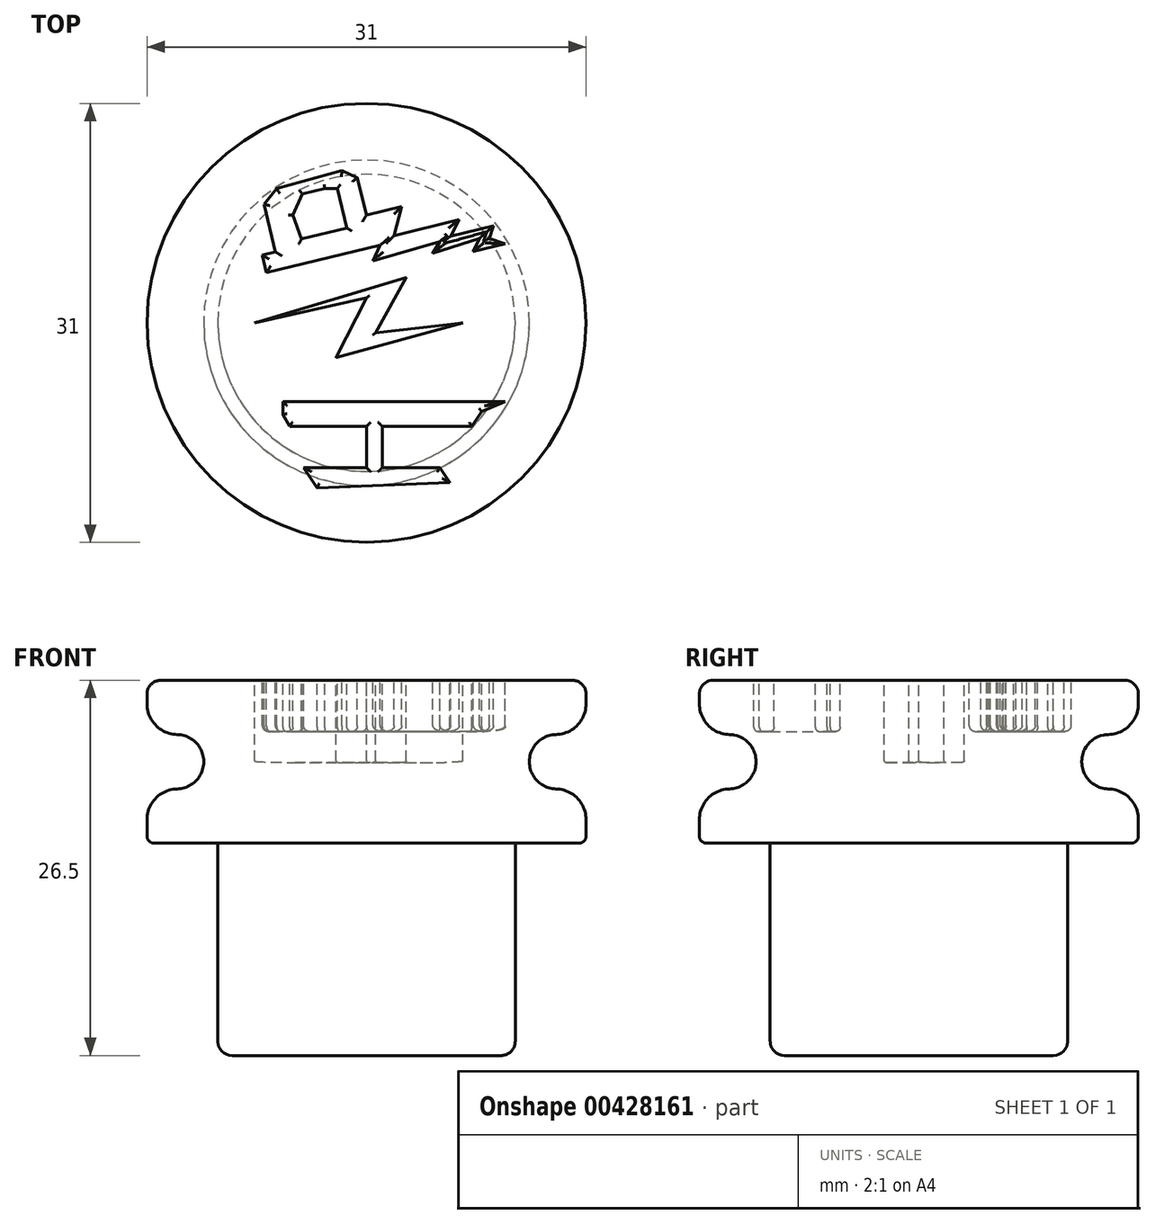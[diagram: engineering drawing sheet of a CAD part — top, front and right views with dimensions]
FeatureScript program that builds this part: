
annotation { "Feature Type Name" : "Feature", "Feature Type Description" : "" }
export const myFeature = defineFeature(function(context is Context, id is Id, definition is map)
    precondition{}
    {
        {
            var Q0;
            Q0=qCreatedBy(makeId("Right.planeOp"),FACE);
            var sketch = newSketch(context, id + "F0", { "sketchPlane" : qUnion([Q0])});
            skLineSegment(sketch, "E0", {"start": v(-10.5, -11.5) * mm, "end": v(-10.5, -26.5) * mm});
            skLineSegment(sketch, "E1", {"start": v(-10.5, -26.5) * mm, "end": v(0, -26.5) * mm});
            skLineSegment(sketch, "E2", {"start": v(0, -26.5) * mm, "end": v(0, 0) * mm});
            skLineSegment(sketch, "E3", {"start": v(0, 0) * mm, "end": v(-15.5, 0) * mm});
            skLineSegment(sketch, "E4", {"start": v(-10.5, -11.5) * mm, "end": v(-15.5, -11.5) * mm});
            skLineSegment(sketch, "E5", {"start": v(-15.5, -11.5) * mm, "end": v(-15.5, -7.67) * mm});
            skLineSegment(sketch, "E6", {"start": v(-15.5, 0) * mm, "end": v(-15.5, -3.83) * mm});
            skLineSegment(sketch, "E7", {"start": v(-15.5, -3.83) * mm, "end": v(-11.5, -3.83) * mm});
            skLineSegment(sketch, "E8", {"start": v(-11.5, -3.83) * mm, "end": v(-11.5, -7.67) * mm});
            skLineSegment(sketch, "E9", {"start": v(-11.5, -7.67) * mm, "end": v(-15.5, -7.67) * mm});
            skSolve(sketch);
        }
        {
            var Q0;
            Q0 = qSketchRegion(id + "F0", true);
            var Q1;
            Q1=sQuery(id+"F0.wireOp",EDGE,"E2");
            revolve(context, id + "F1", {"entities" : qUnion([Q0]), "axis" : qUnion([Q1]), "revolveType" : RevolveType.FULL});
        }
        {
            var Q0;
            Q0=makeQuery(id+"F1.opRevolve","SWEPT_EDGE",EDGE,{"disambiguationData":[OSD([sQuery(id+"F0.wireOp",EDGE,"E7"),sQuery(id+"F0.wireOp",EDGE,"E8")])]});
            var Q1;
            Q1=makeQuery(id+"F1.opRevolve","SWEPT_EDGE",EDGE,{"disambiguationData":[OSD([sQuery(id+"F0.wireOp",EDGE,"E8"),sQuery(id+"F0.wireOp",EDGE,"E9")])]});
            fillet(context, id + "F2", {"entities" : qUnion([Q0, Q1]), "radius" : 1.9 * mm, "tangentPropagation" : true, "allowEdgeOverflow" : false});
        }
        {
            var Q0;
            Q0=makeQuery(id+"F1.opRevolve","SWEPT_EDGE",EDGE,{"disambiguationData":[OSD([sQuery(id+"F0.wireOp",EDGE,"E6"),sQuery(id+"F0.wireOp",EDGE,"E7")])]});
            var Q1;
            Q1=makeQuery(id+"F1.opRevolve","SWEPT_EDGE",EDGE,{"disambiguationData":[OSD([sQuery(id+"F0.wireOp",EDGE,"E5"),sQuery(id+"F0.wireOp",EDGE,"E9")])]});
            fillet(context, id + "F3", {"entities" : qUnion([Q0, Q1]), "radius" : 2.17 * mm, "tangentPropagation" : true, "allowEdgeOverflow" : false});
        }
        {
            var Q0;
            Q0=makeQuery(id+"F1.opRevolve","SWEPT_EDGE",EDGE,{"disambiguationData":[OSD([sQuery(id+"F0.wireOp",EDGE,"E3"),sQuery(id+"F0.wireOp",EDGE,"E6")])]});
            fillet(context, id + "F4", {"entities" : qUnion([Q0]), "radius" : 0.97 * mm, "tangentPropagation" : true, "allowEdgeOverflow" : false});
        }
        {
            var Q0;
            Q0=makeQuery(id+"F1.opRevolve","SWEPT_EDGE",EDGE,{"disambiguationData":[OSD([sQuery(id+"F0.wireOp",EDGE,"E4"),sQuery(id+"F0.wireOp",EDGE,"E5")])]});
            fillet(context, id + "F5", {"entities" : qUnion([Q0]), "radius" : 0.5 * mm, "tangentPropagation" : true, "allowEdgeOverflow" : false});
        }
        {
            var Q0;
            Q0=makeQuery(id+"F1.opRevolve","SWEPT_FACE",FACE,{"disambiguationData":[OSD([sQuery(id+"F0.wireOp",EDGE,"E3")])]});
            var sketch = newSketch(context, id + "F6", { "sketchPlane" : qUnion([Q0])});
            skLineSegment(sketch, "E10", {"start": v(-7.9, 0) * mm, "end": v(0, 1.76) * mm});
            skLineSegment(sketch, "E11", {"start": v(2.8, 3.2) * mm, "end": v(-7.9, 0) * mm});
            skLineSegment(sketch, "E12", {"start": v(0, 1.76) * mm, "end": v(-2.15, -2.44) * mm});
            skLineSegment(sketch, "E13", {"start": v(-2.15, -2.44) * mm, "end": v(6.79, 0) * mm});
            skLineSegment(sketch, "E14", {"start": v(2.8, 3.2) * mm, "end": v(0.64, -0.7) * mm});
            skLineSegment(sketch, "E15", {"start": v(0.64, -0.7) * mm, "end": v(6.79, 0) * mm});
            skSolve(sketch);
        }
        {
            var Q0;
            Q0 = qSketchRegion(id + "F6", true);
            extrude(context, id + "F7", {"entities" : qUnion([Q0]), "operationType" : NewBodyOperationType.REMOVE, "oppositeDirection" : true, "depth" : 5.8 * mm});
        }
        {
            var Q0;
            Q0=makeQuery(id+"F7.boolean.opBoolean","COPY",EDGE,{"derivedFrom":makeQuery(id+"F7.opExtrude","CAP_EDGE",EDGE,{"disambiguationData":[OSD([sQuery(id+"F6.wireOp",EDGE,"E12")])],"isStart":false})});
            var Q1;
            Q1=makeQuery(id+"F7.boolean.opBoolean","COPY",EDGE,{"derivedFrom":makeQuery(id+"F7.opExtrude","CAP_EDGE",EDGE,{"disambiguationData":[OSD([sQuery(id+"F6.wireOp",EDGE,"E13")])],"isStart":false})});
            var Q2;
            Q2=makeQuery(id+"F7.boolean.opBoolean","COPY",EDGE,{"derivedFrom":makeQuery(id+"F7.opExtrude","CAP_EDGE",EDGE,{"disambiguationData":[OSD([sQuery(id+"F6.wireOp",EDGE,"E14")])],"isStart":false})});
            var Q3;
            Q3=makeQuery(id+"F7.boolean.opBoolean","COPY",EDGE,{"derivedFrom":makeQuery(id+"F7.opExtrude","CAP_EDGE",EDGE,{"disambiguationData":[OSD([sQuery(id+"F6.wireOp",EDGE,"E15")])],"isStart":false})});
            var Q4;
            Q4=makeQuery(id+"F7.boolean.opBoolean","COPY",EDGE,{"derivedFrom":makeQuery(id+"F7.opExtrude","CAP_EDGE",EDGE,{"disambiguationData":[OSD([sQuery(id+"F6.wireOp",EDGE,"E11")])],"isStart":false})});
            var Q5;
            Q5=makeQuery(id+"F7.boolean.opBoolean","COPY",EDGE,{"derivedFrom":makeQuery(id+"F7.opExtrude","CAP_EDGE",EDGE,{"disambiguationData":[OSD([sQuery(id+"F6.wireOp",EDGE,"E10")])],"isStart":false})});
            fillet(context, id + "F8", {"entities" : qUnion([Q0, Q1, Q2, Q3, Q4, Q5]), "radius" : 0.1 * mm, "tangentPropagation" : true, "allowEdgeOverflow" : false});
        }
        {
            var Q0;
            Q0=makeQuery(id+"F1.opRevolve","SWEPT_FACE",FACE,{"disambiguationData":[OSD([sQuery(id+"F0.wireOp",EDGE,"E3")])]});
            var sketch = newSketch(context, id + "F9", { "sketchPlane" : qUnion([Q0])});
            skLineSegment(sketch, "E16", {"start": v(-3.5, -11.65) * mm, "end": v(-4.43, -10.22) * mm});
            skLineSegment(sketch, "E17", {"start": v(-4.43, -10.22) * mm, "end": v(5.17, -10.22) * mm});
            skLineSegment(sketch, "E18", {"start": v(5.17, -10.22) * mm, "end": v(5.89, -11.27) * mm});
            skLineSegment(sketch, "E19", {"start": v(5.89, -11.27) * mm, "end": v(-3.5, -11.65) * mm});
            skLineSegment(sketch, "E20", {"start": v(0, -10.22) * mm, "end": v(0, -7.31) * mm});
            skLineSegment(sketch, "E21", {"start": v(0, -7.31) * mm, "end": v(1.11, -7.31) * mm});
            skLineSegment(sketch, "E22", {"start": v(1.11, -7.31) * mm, "end": v(1.11, -10.22) * mm});
            skLineSegment(sketch, "E23", {"start": v(0, -7.31) * mm, "end": v(-5.42, -7.31) * mm});
            skLineSegment(sketch, "E24", {"start": v(-5.42, -7.31) * mm, "end": v(-5.91, -6.5) * mm});
            skLineSegment(sketch, "E25", {"start": v(-5.91, -6.5) * mm, "end": v(-5.91, -5.56) * mm});
            skLineSegment(sketch, "E26", {"start": v(-5.91, -5.56) * mm, "end": v(9.78, -5.56) * mm});
            skLineSegment(sketch, "E27", {"start": v(9.78, -5.56) * mm, "end": v(8.14, -6.27) * mm});
            skLineSegment(sketch, "E28", {"start": v(8.14, -6.27) * mm, "end": v(7.42, -7.31) * mm});
            skLineSegment(sketch, "E29", {"start": v(7.42, -7.31) * mm, "end": v(1.11, -7.31) * mm});
            skLineSegment(sketch, "E30", {"start": v(9.78, 5.58) * mm, "end": v(7.53, 5.03) * mm});
            skLineSegment(sketch, "E31", {"start": v(7.53, 5.03) * mm, "end": v(7.97, 5.97) * mm});
            skLineSegment(sketch, "E32", {"start": v(7.97, 5.97) * mm, "end": v(4.68, 4.92) * mm});
            skLineSegment(sketch, "E33", {"start": v(4.68, 4.92) * mm, "end": v(5.17, 5.75) * mm});
            skLineSegment(sketch, "E34", {"start": v(5.17, 5.75) * mm, "end": v(0.45, 4.38) * mm});
            skLineSegment(sketch, "E35", {"start": v(0.45, 4.38) * mm, "end": v(0.95, 5.47) * mm});
            skLineSegment(sketch, "E36", {"start": v(0.95, 5.47) * mm, "end": v(-7.06, 3.55) * mm});
            skLineSegment(sketch, "E37", {"start": v(9.78, 5.58) * mm, "end": v(8.66, 5.97) * mm});
            skPoint(sketch, "E37.endSnap0", {"position": v(8.66, 5.3) * mm});
            skLineSegment(sketch, "E38", {"start": v(8.66, 5.97) * mm, "end": v(8.96, 6.86) * mm});
            skLineSegment(sketch, "E39", {"start": v(8.96, 6.86) * mm, "end": v(5.93, 6.12) * mm});
            skLineSegment(sketch, "E40", {"start": v(5.93, 6.12) * mm, "end": v(6.55, 7.28) * mm});
            skLineSegment(sketch, "E41", {"start": v(6.55, 7.28) * mm, "end": v(1.96, 6.16) * mm});
            skLineSegment(sketch, "E42", {"start": v(1.96, 6.16) * mm, "end": v(2.48, 8.22) * mm});
            skLineSegment(sketch, "E43", {"start": v(2.48, 8.22) * mm, "end": v(0, 7.61) * mm});
            skLineSegment(sketch, "E44", {"start": v(-7.06, 3.55) * mm, "end": v(-7.36, 4.8) * mm});
            skLineSegment(sketch, "E45", {"start": v(-7.36, 4.8) * mm, "end": v(-6.44, 5.01) * mm});
            skLineSegment(sketch, "E46", {"start": v(-6.44, 5.01) * mm, "end": v(-7.25, 8.38) * mm});
            skLineSegment(sketch, "E47", {"start": v(-7.25, 8.38) * mm, "end": v(-6.35, 9.48) * mm});
            skLineSegment(sketch, "E48", {"start": v(0, 7.61) * mm, "end": v(-0.65, 10.26) * mm});
            skLineSegment(sketch, "E49", {"start": v(-0.65, 10.26) * mm, "end": v(-1.74, 10.74) * mm});
            skLineSegment(sketch, "E50", {"start": v(-1.74, 10.74) * mm, "end": v(-6.35, 9.48) * mm});
            skLineSegment(sketch, "E51", {"start": v(-4.6, 5.91) * mm, "end": v(-1.39, 6.7) * mm});
            skLineSegment(sketch, "E52", {"start": v(-1.39, 6.7) * mm, "end": v(-2.07, 9.48) * mm});
            skLineSegment(sketch, "E53", {"start": v(-2.07, 9.48) * mm, "end": v(-2.95, 9.48) * mm});
            skLineSegment(sketch, "E54", {"start": v(-2.95, 9.48) * mm, "end": v(-4.53, 9.1) * mm});
            skLineSegment(sketch, "E55", {"start": v(-4.53, 9.1) * mm, "end": v(-5.2, 7.61) * mm});
            skLineSegment(sketch, "E56", {"start": v(-5.2, 7.61) * mm, "end": v(-4.6, 5.91) * mm});
            skSolve(sketch);
        }
        {
            var Q0;
            Q0=makeQuery(id+"F9.imprint","IMPRINT",FACE,{"disambiguationData":[TD([[makeQuery(id+"F9.imprint","IMPRINT",EDGE,{"derivedFrom":sQuery(id+"F9.wireOp",EDGE,"E30")}),-1.0]])]});
            var Q1;
            Q1=makeQuery(id+"F9.imprint","IMPRINT",FACE,{"disambiguationData":[TD([[makeQuery(id+"F9.imprint","IMPRINT",EDGE,{"derivedFrom":sQuery(id+"F9.wireOp",EDGE,"E21")}),1.0]])]});
            var Q2;
            {var subQ0=sQuery(id+"F9.wireOp",EDGE,"E20");Q2=makeQuery(id+"F9.imprint","IMPRINT",FACE,{"disambiguationData":[TD([[makeQuery(id+"F9.imprint","IMPRINT",EDGE,{"derivedFrom":subQ0}),-1.0]])]});}
            var Q3;
            {var subQ4=sQuery(id+"F9.wireOp",EDGE,"E16");Q3=makeQuery(id+"F9.imprint","IMPRINT",FACE,{"disambiguationData":[TD([[makeQuery(id+"F9.imprint","IMPRINT",EDGE,{"derivedFrom":subQ4}),-1.0]])]});}
            extrude(context, id + "F10", {"entities" : qUnion([Q0, Q1, Q2, Q3]), "operationType" : NewBodyOperationType.REMOVE, "oppositeDirection" : true, "depth" : 3.6 * mm});
        }
        {
            var Q0;
            Q0=makeQuery(id+"F1.opRevolve","SWEPT_EDGE",EDGE,{"disambiguationData":[OSD([sQuery(id+"F0.wireOp",EDGE,"E0"),sQuery(id+"F0.wireOp",EDGE,"E1")])]});
            fillet(context, id + "F11", {"entities" : qUnion([Q0]), "radius" : 1 * mm, "tangentPropagation" : true, "allowEdgeOverflow" : false});
        }
        {
            var Q0;
            Q0=makeQuery(id+"F10.boolean.opBoolean","COPY",EDGE,{"derivedFrom":makeQuery(id+"F10.opExtrude","CAP_EDGE",EDGE,{"disambiguationData":[OSD([sQuery(id+"F9.wireOp",EDGE,"E51")])],"isStart":true})});
            var Q1;
            Q1=makeQuery(id+"F10.boolean.opBoolean","COPY",EDGE,{"derivedFrom":makeQuery(id+"F10.opExtrude","CAP_EDGE",EDGE,{"disambiguationData":[OSD([sQuery(id+"F9.wireOp",EDGE,"E52")])],"isStart":true})});
            var Q2;
            Q2=makeQuery(id+"F10.boolean.opBoolean","COPY",EDGE,{"derivedFrom":makeQuery(id+"F10.opExtrude","CAP_EDGE",EDGE,{"disambiguationData":[OSD([sQuery(id+"F9.wireOp",EDGE,"E53")])],"isStart":true})});
            var Q3;
            Q3=makeQuery(id+"F10.boolean.opBoolean","COPY",EDGE,{"derivedFrom":makeQuery(id+"F10.opExtrude","CAP_EDGE",EDGE,{"disambiguationData":[OSD([sQuery(id+"F9.wireOp",EDGE,"E54")])],"isStart":true})});
            var Q4;
            Q4=makeQuery(id+"F10.boolean.opBoolean","COPY",EDGE,{"derivedFrom":makeQuery(id+"F10.opExtrude","CAP_EDGE",EDGE,{"disambiguationData":[OSD([sQuery(id+"F9.wireOp",EDGE,"E55")])],"isStart":true})});
            var Q5;
            Q5=makeQuery(id+"F10.boolean.opBoolean","COPY",EDGE,{"derivedFrom":makeQuery(id+"F10.opExtrude","CAP_EDGE",EDGE,{"disambiguationData":[OSD([sQuery(id+"F9.wireOp",EDGE,"E56")])],"isStart":true})});
            var Q6;
            Q6=makeQuery(id+"F10.boolean.opBoolean","COPY",EDGE,{"derivedFrom":makeQuery(id+"F10.opExtrude","CAP_EDGE",EDGE,{"disambiguationData":[OSD([sQuery(id+"F9.wireOp",EDGE,"E56")])],"isStart":false})});
            var Q7;
            Q7=makeQuery(id+"F10.boolean.opBoolean","COPY",EDGE,{"derivedFrom":makeQuery(id+"F10.opExtrude","CAP_EDGE",EDGE,{"disambiguationData":[OSD([sQuery(id+"F9.wireOp",EDGE,"E55")])],"isStart":false})});
            var Q8;
            Q8=makeQuery(id+"F10.boolean.opBoolean","COPY",EDGE,{"derivedFrom":makeQuery(id+"F10.opExtrude","CAP_EDGE",EDGE,{"disambiguationData":[OSD([sQuery(id+"F9.wireOp",EDGE,"E54")])],"isStart":false})});
            var Q9;
            Q9=makeQuery(id+"F10.boolean.opBoolean","COPY",EDGE,{"derivedFrom":makeQuery(id+"F10.opExtrude","CAP_EDGE",EDGE,{"disambiguationData":[OSD([sQuery(id+"F9.wireOp",EDGE,"E53")])],"isStart":false})});
            var Q10;
            Q10=makeQuery(id+"F10.boolean.opBoolean","COPY",EDGE,{"derivedFrom":makeQuery(id+"F10.opExtrude","CAP_EDGE",EDGE,{"disambiguationData":[OSD([sQuery(id+"F9.wireOp",EDGE,"E52")])],"isStart":false})});
            var Q11;
            Q11=makeQuery(id+"F10.boolean.opBoolean","COPY",EDGE,{"derivedFrom":makeQuery(id+"F10.opExtrude","CAP_EDGE",EDGE,{"disambiguationData":[OSD([sQuery(id+"F9.wireOp",EDGE,"E51")])],"isStart":false})});
            fillet(context, id + "F12", {"entities" : qUnion([Q0, Q1, Q2, Q3, Q4, Q5, Q6, Q7, Q8, Q9, Q10, Q11]), "radius" : 0.29 * mm, "tangentPropagation" : true, "allowEdgeOverflow" : false});
        }
        {
            var Q0;
            Q0=makeQuery(id+"F10.boolean.opBoolean","COPY",EDGE,{"derivedFrom":makeQuery(id+"F10.opExtrude","CAP_EDGE",EDGE,{"disambiguationData":[OSD([sQuery(id+"F9.wireOp",EDGE,"E36")])],"isStart":false})});
            var Q1;
            Q1=makeQuery(id+"F10.boolean.opBoolean","COPY",EDGE,{"derivedFrom":makeQuery(id+"F10.opExtrude","CAP_EDGE",EDGE,{"disambiguationData":[OSD([sQuery(id+"F9.wireOp",EDGE,"E46")])],"isStart":false})});
            var Q2;
            Q2=makeQuery(id+"F10.boolean.opBoolean","COPY",EDGE,{"derivedFrom":makeQuery(id+"F10.opExtrude","CAP_EDGE",EDGE,{"disambiguationData":[OSD([sQuery(id+"F9.wireOp",EDGE,"E44")])],"isStart":false})});
            var Q3;
            Q3=makeQuery(id+"F10.boolean.opBoolean","COPY",EDGE,{"derivedFrom":makeQuery(id+"F10.opExtrude","CAP_EDGE",EDGE,{"disambiguationData":[OSD([sQuery(id+"F9.wireOp",EDGE,"E45")])],"isStart":false})});
            var Q4;
            Q4=makeQuery(id+"F10.boolean.opBoolean","COPY",EDGE,{"derivedFrom":makeQuery(id+"F10.opExtrude","CAP_EDGE",EDGE,{"disambiguationData":[OSD([sQuery(id+"F9.wireOp",EDGE,"E47")])],"isStart":false})});
            var Q5;
            Q5=makeQuery(id+"F10.boolean.opBoolean","COPY",EDGE,{"derivedFrom":makeQuery(id+"F10.opExtrude","CAP_EDGE",EDGE,{"disambiguationData":[OSD([sQuery(id+"F9.wireOp",EDGE,"E50")])],"isStart":false})});
            var Q6;
            Q6=makeQuery(id+"F10.boolean.opBoolean","COPY",EDGE,{"derivedFrom":makeQuery(id+"F10.opExtrude","CAP_EDGE",EDGE,{"disambiguationData":[OSD([sQuery(id+"F9.wireOp",EDGE,"E48")])],"isStart":false})});
            var Q7;
            Q7=makeQuery(id+"F10.boolean.opBoolean","COPY",EDGE,{"derivedFrom":makeQuery(id+"F10.opExtrude","CAP_EDGE",EDGE,{"disambiguationData":[OSD([sQuery(id+"F9.wireOp",EDGE,"E49")])],"isStart":false})});
            var Q8;
            Q8=makeQuery(id+"F10.boolean.opBoolean","COPY",EDGE,{"derivedFrom":makeQuery(id+"F10.opExtrude","CAP_EDGE",EDGE,{"disambiguationData":[OSD([sQuery(id+"F9.wireOp",EDGE,"E43")])],"isStart":false})});
            var Q9;
            Q9=makeQuery(id+"F10.boolean.opBoolean","COPY",EDGE,{"derivedFrom":makeQuery(id+"F10.opExtrude","CAP_EDGE",EDGE,{"disambiguationData":[OSD([sQuery(id+"F9.wireOp",EDGE,"E42")])],"isStart":false})});
            var Q10;
            Q10=makeQuery(id+"F10.boolean.opBoolean","COPY",EDGE,{"derivedFrom":makeQuery(id+"F10.opExtrude","CAP_EDGE",EDGE,{"disambiguationData":[OSD([sQuery(id+"F9.wireOp",EDGE,"E41")])],"isStart":false})});
            var Q11;
            Q11=makeQuery(id+"F10.boolean.opBoolean","COPY",EDGE,{"derivedFrom":makeQuery(id+"F10.opExtrude","CAP_EDGE",EDGE,{"disambiguationData":[OSD([sQuery(id+"F9.wireOp",EDGE,"E39")])],"isStart":false})});
            var Q12;
            Q12=makeQuery(id+"F10.boolean.opBoolean","COPY",EDGE,{"derivedFrom":makeQuery(id+"F10.opExtrude","CAP_EDGE",EDGE,{"disambiguationData":[OSD([sQuery(id+"F9.wireOp",EDGE,"E40")])],"isStart":false})});
            var Q13;
            Q13=makeQuery(id+"F10.boolean.opBoolean","COPY",EDGE,{"derivedFrom":makeQuery(id+"F10.opExtrude","CAP_EDGE",EDGE,{"disambiguationData":[OSD([sQuery(id+"F9.wireOp",EDGE,"E38")])],"isStart":false})});
            var Q14;
            Q14=makeQuery(id+"F10.boolean.opBoolean","COPY",EDGE,{"derivedFrom":makeQuery(id+"F10.opExtrude","CAP_EDGE",EDGE,{"disambiguationData":[OSD([sQuery(id+"F9.wireOp",EDGE,"E37")])],"isStart":false})});
            var Q15;
            Q15=makeQuery(id+"F10.boolean.opBoolean","COPY",EDGE,{"derivedFrom":makeQuery(id+"F10.opExtrude","CAP_EDGE",EDGE,{"disambiguationData":[OSD([sQuery(id+"F9.wireOp",EDGE,"E30")])],"isStart":false})});
            var Q16;
            Q16=makeQuery(id+"F10.boolean.opBoolean","COPY",EDGE,{"derivedFrom":makeQuery(id+"F10.opExtrude","CAP_EDGE",EDGE,{"disambiguationData":[OSD([sQuery(id+"F9.wireOp",EDGE,"E31")])],"isStart":false})});
            var Q17;
            Q17=makeQuery(id+"F10.boolean.opBoolean","COPY",EDGE,{"derivedFrom":makeQuery(id+"F10.opExtrude","CAP_EDGE",EDGE,{"disambiguationData":[OSD([sQuery(id+"F9.wireOp",EDGE,"E32")])],"isStart":false})});
            var Q18;
            Q18=makeQuery(id+"F10.boolean.opBoolean","COPY",EDGE,{"derivedFrom":makeQuery(id+"F10.opExtrude","CAP_EDGE",EDGE,{"disambiguationData":[OSD([sQuery(id+"F9.wireOp",EDGE,"E33")])],"isStart":false})});
            var Q19;
            Q19=makeQuery(id+"F10.boolean.opBoolean","COPY",EDGE,{"derivedFrom":makeQuery(id+"F10.opExtrude","CAP_EDGE",EDGE,{"disambiguationData":[OSD([sQuery(id+"F9.wireOp",EDGE,"E34")])],"isStart":false})});
            var Q20;
            Q20=makeQuery(id+"F10.boolean.opBoolean","COPY",EDGE,{"derivedFrom":makeQuery(id+"F10.opExtrude","CAP_EDGE",EDGE,{"disambiguationData":[OSD([sQuery(id+"F9.wireOp",EDGE,"E35")])],"isStart":false})});
            fillet(context, id + "F13", {"entities" : qUnion([Q0, Q1, Q2, Q3, Q4, Q5, Q6, Q7, Q8, Q9, Q10, Q11, Q12, Q13, Q14, Q15, Q16, Q17, Q18, Q19, Q20]), "radius" : 0.4 * mm, "tangentPropagation" : true, "allowEdgeOverflow" : false});
        }
        {
            var Q0;
            Q0=makeQuery(id+"F10.boolean.opBoolean","COPY",EDGE,{"derivedFrom":makeQuery(id+"F10.opExtrude","CAP_EDGE",EDGE,{"disambiguationData":[OSD([sQuery(id+"F9.wireOp",EDGE,"E23")])],"isStart":false})});
            var Q1;
            Q1=makeQuery(id+"F10.boolean.opBoolean","COPY",EDGE,{"derivedFrom":makeQuery(id+"F10.opExtrude","CAP_EDGE",EDGE,{"disambiguationData":[OSD([sQuery(id+"F9.wireOp",EDGE,"E20")])],"isStart":false})});
            var Q2;
            Q2=makeQuery(id+"F10.boolean.opBoolean","COPY",EDGE,{"derivedFrom":makeQuery(id+"F10.opExtrude","CAP_EDGE",EDGE,{"disambiguationData":[OSD([sQuery(id+"F9.wireOp",EDGE,"E16")])],"isStart":false})});
            var Q3;
            {var subQ0=sQuery(id+"F9.wireOp",EDGE,"E17");Q3=makeQuery(id+"F10.boolean.opBoolean","COPY",EDGE,{"derivedFrom":makeQuery(id+"F10.opExtrude","CAP_EDGE",EDGE,{"disambiguationData":[OSD([subQ0]),TDD([makeQuery(id+"F9.imprint","IMPRINT",EDGE,{"disambiguationData":[TD([[makeQuery(id+"F9.imprint","INTERSECT",VERTEX,{"derivedFrom":[sQuery(id+"F9.wireOp",EDGE,"E16"),subQ0]}),-1.0]])],"derivedFrom":subQ0})])],"isStart":false})});}
            var Q4;
            Q4=makeQuery(id+"F10.boolean.opBoolean","COPY",EDGE,{"derivedFrom":makeQuery(id+"F10.opExtrude","CAP_EDGE",EDGE,{"disambiguationData":[OSD([sQuery(id+"F9.wireOp",EDGE,"E19")])],"isStart":false})});
            var Q5;
            Q5=makeQuery(id+"F10.boolean.opBoolean","COPY",EDGE,{"derivedFrom":makeQuery(id+"F10.opExtrude","CAP_EDGE",EDGE,{"disambiguationData":[OSD([sQuery(id+"F9.wireOp",EDGE,"E18")])],"isStart":false})});
            var Q6;
            {var subQ0=sQuery(id+"F9.wireOp",EDGE,"E17");Q6=makeQuery(id+"F10.boolean.opBoolean","COPY",EDGE,{"derivedFrom":makeQuery(id+"F10.opExtrude","CAP_EDGE",EDGE,{"disambiguationData":[OSD([subQ0]),TDD([makeQuery(id+"F9.imprint","IMPRINT",EDGE,{"disambiguationData":[TD([[makeQuery(id+"F9.imprint","INTERSECT",VERTEX,{"derivedFrom":[subQ0,sQuery(id+"F9.wireOp",EDGE,"E18")]}),1.0]])],"derivedFrom":subQ0})])],"isStart":false})});}
            var Q7;
            Q7=makeQuery(id+"F10.boolean.opBoolean","COPY",EDGE,{"derivedFrom":makeQuery(id+"F10.opExtrude","CAP_EDGE",EDGE,{"disambiguationData":[OSD([sQuery(id+"F9.wireOp",EDGE,"E22")])],"isStart":false})});
            var Q8;
            Q8=makeQuery(id+"F10.boolean.opBoolean","COPY",EDGE,{"derivedFrom":makeQuery(id+"F10.opExtrude","CAP_EDGE",EDGE,{"disambiguationData":[OSD([sQuery(id+"F9.wireOp",EDGE,"E29")])],"isStart":false})});
            var Q9;
            Q9=makeQuery(id+"F10.boolean.opBoolean","COPY",EDGE,{"derivedFrom":makeQuery(id+"F10.opExtrude","CAP_EDGE",EDGE,{"disambiguationData":[OSD([sQuery(id+"F9.wireOp",EDGE,"E28")])],"isStart":false})});
            var Q10;
            Q10=makeQuery(id+"F10.boolean.opBoolean","COPY",EDGE,{"derivedFrom":makeQuery(id+"F10.opExtrude","CAP_EDGE",EDGE,{"disambiguationData":[OSD([sQuery(id+"F9.wireOp",EDGE,"E27")])],"isStart":false})});
            var Q11;
            Q11=makeQuery(id+"F10.boolean.opBoolean","COPY",EDGE,{"derivedFrom":makeQuery(id+"F10.opExtrude","CAP_EDGE",EDGE,{"disambiguationData":[OSD([sQuery(id+"F9.wireOp",EDGE,"E26")])],"isStart":false})});
            var Q12;
            Q12=makeQuery(id+"F10.boolean.opBoolean","COPY",EDGE,{"derivedFrom":makeQuery(id+"F10.opExtrude","CAP_EDGE",EDGE,{"disambiguationData":[OSD([sQuery(id+"F9.wireOp",EDGE,"E24")])],"isStart":false})});
            var Q13;
            Q13=makeQuery(id+"F10.boolean.opBoolean","COPY",EDGE,{"derivedFrom":makeQuery(id+"F10.opExtrude","CAP_EDGE",EDGE,{"disambiguationData":[OSD([sQuery(id+"F9.wireOp",EDGE,"E25")])],"isStart":false})});
            fillet(context, id + "F14", {"entities" : qUnion([Q0, Q1, Q2, Q3, Q4, Q5, Q6, Q7, Q8, Q9, Q10, Q11, Q12, Q13]), "radius" : 0.3 * mm, "tangentPropagation" : true, "allowEdgeOverflow" : false});
        }
    });
